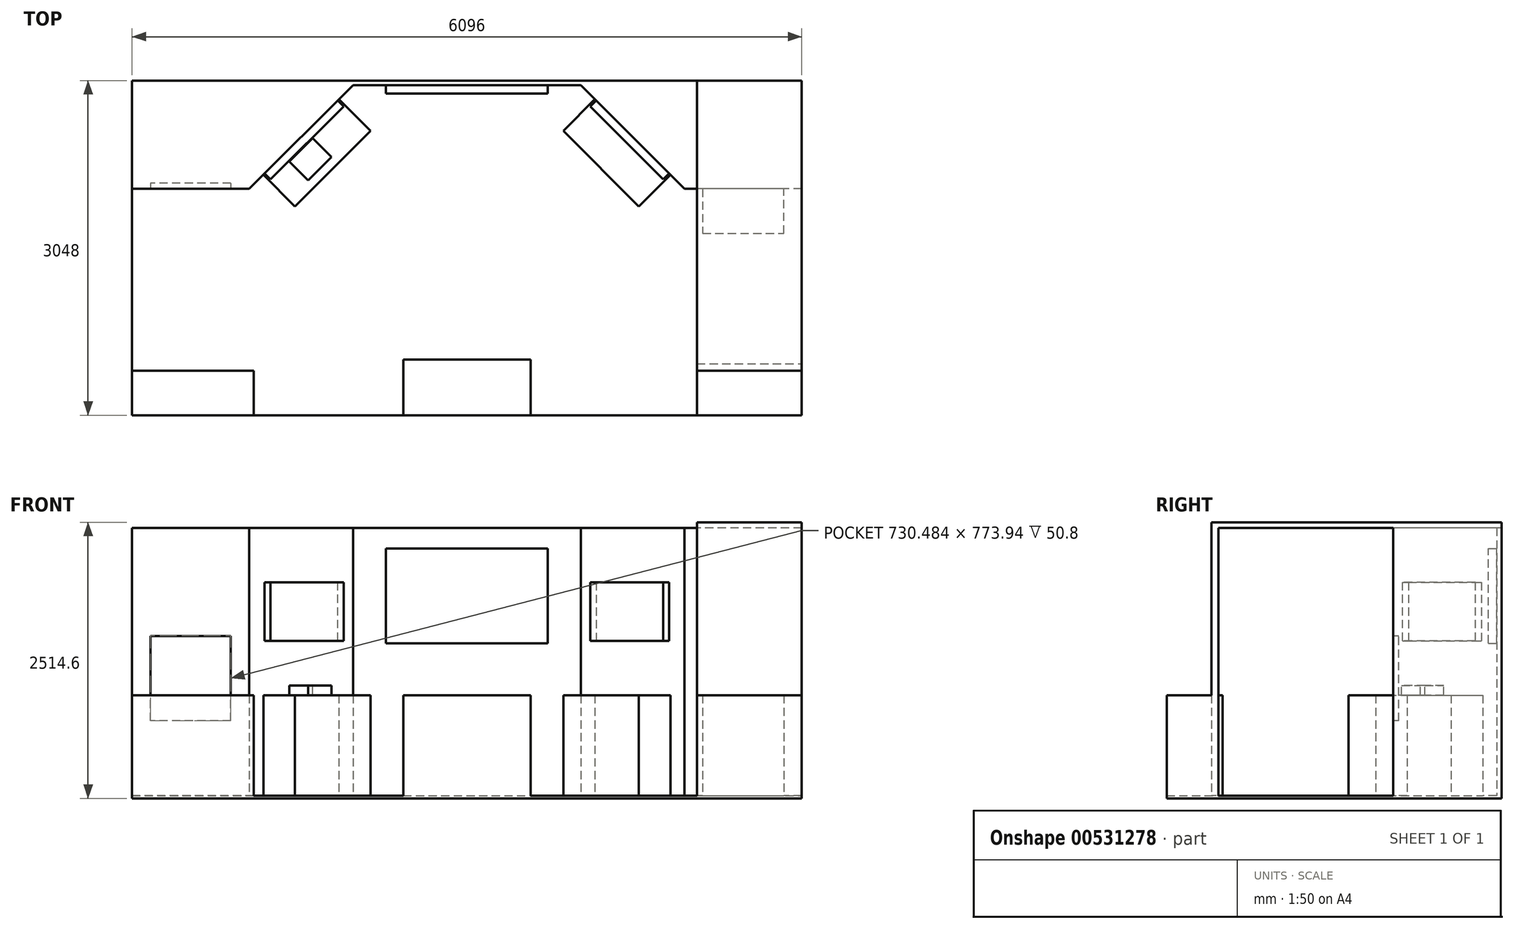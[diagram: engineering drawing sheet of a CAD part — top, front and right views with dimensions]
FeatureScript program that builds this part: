
annotation { "Feature Type Name" : "Feature", "Feature Type Description" : "" }
export const myFeature = defineFeature(function(context is Context, id is Id, definition is map)
    precondition{}
    {
        {
            var Q0;
            Q0=qCreatedBy(makeId("Top.planeOp"),FACE);
            var sketch = newSketch(context, id + "F0", { "sketchPlane" : qUnion([Q0])});
            skLineSegment(sketch, "E0.bottom", {"start": v(3048, 1524) * mm, "end": v(-3048, 1524) * mm});
            skLineSegment(sketch, "E0.top", {"start": v(3048, -1524) * mm, "end": v(-3048, -1524) * mm});
            skLineSegment(sketch, "E0.left", {"start": v(3048, 1524) * mm, "end": v(3048, -1524) * mm});
            skLineSegment(sketch, "E0.right", {"start": v(-3048, 1524) * mm, "end": v(-3048, -1524) * mm});
            skPoint(sketch, "E0.middle", {"position": v(0, 0) * mm});
            skSolve(sketch);
        }
        {
            var Q0;
            Q0=makeQuery(id+"F0.imprint","IMPRINT",FACE,{"disambiguationData":[TD([[makeQuery(id+"F0.imprint","IMPRINT",EDGE,{"derivedFrom":sQuery(id+"F0.wireOp",EDGE,"E0.bottom")}),1.0]])]});
            var sketch = newSketch(context, id + "F1", { "sketchPlane" : qUnion([Q0])});
            skLineSegment(sketch, "E1", {"start": v(3048, 1524) * mm, "end": v(-3048, 1524) * mm});
            skLineSegment(sketch, "E2", {"start": v(-3048, 1524) * mm, "end": v(-3048, 537.06) * mm});
            skLineSegment(sketch, "E3", {"start": v(-3048, 537.06) * mm, "end": v(-1981.2, 537.06) * mm});
            skLineSegment(sketch, "E4", {"start": v(-1981.2, 537.06) * mm, "end": v(-1037.42, 1480.84) * mm});
            skLineSegment(sketch, "E5", {"start": v(-1037.42, 1480.84) * mm, "end": v(1037.42, 1480.84) * mm});
            skLineSegment(sketch, "E6", {"start": v(1037.42, 1480.84) * mm, "end": v(1981.2, 537.06) * mm});
            skLineSegment(sketch, "E7", {"start": v(3048, 1524) * mm, "end": v(3048, 537.06) * mm});
            skLineSegment(sketch, "E8", {"start": v(3048, 537.06) * mm, "end": v(1981.2, 537.06) * mm});
            skLineSegment(sketch, "E9", {"start": v(0, 0) * mm, "end": v(0, 1480.84) * mm, "construction": true});
            skLineSegment(sketch, "E10", {"start": v(-1853.34, 664.91) * mm, "end": v(-1565.97, 377.55) * mm});
            skLineSegment(sketch, "E11", {"start": v(-1565.97, 377.55) * mm, "end": v(-877.9, 1065.61) * mm});
            skLineSegment(sketch, "E12", {"start": v(-877.9, 1065.61) * mm, "end": v(-1165.27, 1352.98) * mm});
            skLineSegment(sketch, "E13", {"start": v(1165.27, 1352.98) * mm, "end": v(877.9, 1065.61) * mm});
            skLineSegment(sketch, "E14", {"start": v(877.9, 1065.61) * mm, "end": v(1565.97, 377.55) * mm});
            skLineSegment(sketch, "E15", {"start": v(1565.97, 377.55) * mm, "end": v(1853.34, 664.91) * mm});
            skLineSegment(sketch, "E16", {"start": v(2145.45, 537.06) * mm, "end": v(2145.45, 130.66) * mm});
            skLineSegment(sketch, "E17", {"start": v(2145.45, 130.66) * mm, "end": v(2883.75, 130.66) * mm});
            skLineSegment(sketch, "E18", {"start": v(2883.75, 130.66) * mm, "end": v(2883.75, 537.06) * mm});
            skLineSegment(sketch, "E19", {"start": v(-1509.3, 1008.95) * mm, "end": v(-1221.94, 721.58) * mm, "construction": true});
            skLineSegment(sketch, "E20", {"start": v(1509.3, 1008.95) * mm, "end": v(1221.94, 721.58) * mm, "construction": true});
            skLineSegment(sketch, "E21", {"start": v(2514.6, 537.06) * mm, "end": v(2514.6, 130.66) * mm, "construction": true});
            skLineSegment(sketch, "E22.bottom", {"start": v(3048, -1524) * mm, "end": v(2094.08, -1524) * mm});
            skLineSegment(sketch, "E22.top", {"start": v(3048, -648) * mm, "end": v(2094.08, -648) * mm});
            skLineSegment(sketch, "E22.left", {"start": v(3048, -1524) * mm, "end": v(3048, -648) * mm});
            skLineSegment(sketch, "E22.right", {"start": v(2094.08, -1524) * mm, "end": v(2094.08, -648) * mm});
            skLineSegment(sketch, "E23", {"start": v(2094.08, -1086) * mm, "end": v(3048, -1086) * mm, "construction": true});
            skLineSegment(sketch, "E24.bottom", {"start": v(2094.08, -1117.6) * mm, "end": v(3048, -1117.6) * mm});
            skLineSegment(sketch, "E24.top", {"start": v(2094.08, -1054.4) * mm, "end": v(3048, -1054.4) * mm});
            skLineSegment(sketch, "E24.left", {"start": v(2094.08, -1054.4) * mm, "end": v(2094.08, -1117.6) * mm});
            skLineSegment(sketch, "E24.right", {"start": v(3048, -1054.4) * mm, "end": v(3048, -1117.6) * mm});
            skPoint(sketch, "E24.middle", {"position": v(2571.04, -1086) * mm});
            skLineSegment(sketch, "E25.bottom", {"start": v(579.49, -1524) * mm, "end": v(-579.49, -1524) * mm});
            skLineSegment(sketch, "E25.top", {"start": v(579.49, -1016) * mm, "end": v(-579.49, -1016) * mm});
            skLineSegment(sketch, "E25.left", {"start": v(579.49, -1524) * mm, "end": v(579.49, -1016) * mm});
            skLineSegment(sketch, "E25.right", {"start": v(-579.49, -1524) * mm, "end": v(-579.49, -1016) * mm});
            skPoint(sketch, "E25.middle", {"position": v(0, -1270) * mm});
            skLineSegment(sketch, "E26", {"start": v(0, -1270) * mm, "end": v(0, 0) * mm, "construction": true});
            skSolve(sketch);
        }
        {
            var Q0;
            Q0=makeQuery(id+"F1.imprint","IMPRINT",FACE,{"disambiguationData":[TD([[makeQuery(id+"F1.imprint","IMPRINT",EDGE,{"derivedFrom":sQuery(id+"F1.wireOp",EDGE,"E1")}),1.0]])]});
            var Q1;
            Q1=makeQuery(id+"F1.imprint","IMPRINT",FACE,{"disambiguationData":[TD([[makeQuery(id+"F1.imprint","IMPRINT",EDGE,{"derivedFrom":sQuery(id+"F1.wireOp",EDGE,"E24.bottom")}),1.0]])]});
            extrude(context, id + "F2", {"entities" : qUnion([Q0, Q1]), "depth" : 2438.4 * mm, "offsetDistance" : 25.4 * mm});
        }
        {
            var Q0;
            {var subQ0=sQuery(id+"F1.wireOp",EDGE,"E10");Q0=makeQuery(id+"F1.imprint","IMPRINT",FACE,{"disambiguationData":[TD([[makeQuery(id+"F1.imprint","IMPRINT",EDGE,{"derivedFrom":subQ0}),1.0]])]});}
            var Q1;
            Q1=makeQuery(id+"F1.imprint","IMPRINT",FACE,{"disambiguationData":[TD([[makeQuery(id+"F1.imprint","IMPRINT",EDGE,{"derivedFrom":sQuery(id+"F1.wireOp",EDGE,"E25.bottom")}),-1.0]])]});
            var Q2;
            {var subQ0=sQuery(id+"F1.wireOp",EDGE,"E13");Q2=makeQuery(id+"F1.imprint","IMPRINT",FACE,{"disambiguationData":[TD([[makeQuery(id+"F1.imprint","IMPRINT",EDGE,{"derivedFrom":subQ0}),1.0]])]});}
            var Q3;
            {var subQ0=sQuery(id+"F1.wireOp",EDGE,"E16");Q3=makeQuery(id+"F1.imprint","IMPRINT",FACE,{"disambiguationData":[TD([[makeQuery(id+"F1.imprint","IMPRINT",EDGE,{"derivedFrom":subQ0}),1.0]])]});}
            var Q4;
            {var subQ0=sQuery(id+"F1.wireOp",EDGE,"E22.bottom");Q4=makeQuery(id+"F1.imprint","IMPRINT",FACE,{"disambiguationData":[TD([[makeQuery(id+"F1.imprint","IMPRINT",EDGE,{"derivedFrom":subQ0}),-1.0]])]});}
            extrude(context, id + "F3", {"entities" : qUnion([Q0, Q1, Q2, Q3, Q4]), "operationType" : NewBodyOperationType.ADD, "depth" : 914.4 * mm, "offsetDistance" : 25.4 * mm});
        }
        {
            var Q0;
            Q0=makeQuery(id+"F0.imprint","IMPRINT",FACE,{"disambiguationData":[TD([[makeQuery(id+"F0.imprint","IMPRINT",EDGE,{"derivedFrom":sQuery(id+"F0.wireOp",EDGE,"E0.bottom")}),1.0]])]});
            extrude(context, id + "F4", {"entities" : qUnion([Q0]), "operationType" : NewBodyOperationType.ADD, "oppositeDirection" : true, "depth" : 25.4 * mm, "offsetDistance" : 25.4 * mm});
        }
        {
            var Q0;
            Q0=makeQuery(id+"F2.opExtrude","CAP_FACE",FACE,{"disambiguationData":[OSD([sQuery(id+"F1.wireOp",EDGE,"E1"),sQuery(id+"F1.wireOp",EDGE,"E2"),sQuery(id+"F1.wireOp",EDGE,"E3"),sQuery(id+"F1.wireOp",EDGE,"E4"),sQuery(id+"F1.wireOp",EDGE,"E5"),sQuery(id+"F1.wireOp",EDGE,"E6"),sQuery(id+"F1.wireOp",EDGE,"E7"),sQuery(id+"F1.wireOp",EDGE,"E8")])],"isStart":false});
            var sketch = newSketch(context, id + "F5", { "sketchPlane" : qUnion([Q0])});
            skLineSegment(sketch, "E27.bottom", {"start": v(3048, 1524) * mm, "end": v(2094.08, 1524) * mm});
            skLineSegment(sketch, "E27.top", {"start": v(3048, -1117.6) * mm, "end": v(2094.08, -1117.6) * mm});
            skLineSegment(sketch, "E27.left", {"start": v(3048, 1524) * mm, "end": v(3048, -1117.6) * mm});
            skLineSegment(sketch, "E27.right", {"start": v(2094.08, 1524) * mm, "end": v(2094.08, -1117.6) * mm});
            skSolve(sketch);
        }
        {
            var Q0;
            {var subQ0=sQuery(id+"F5.wireOp",EDGE,"E27.top");Q0=makeQuery(id+"F5.imprint","IMPRINT",FACE,{"disambiguationData":[TD([[makeQuery(id+"F5.imprint","IMPRINT",EDGE,{"derivedFrom":subQ0}),-1.0]])]});}
            var Q1;
            {var subQ0=sQuery(id+"F5.wireOp",EDGE,"E27.bottom");Q1=makeQuery(id+"F5.imprint","IMPRINT",FACE,{"disambiguationData":[TD([[makeQuery(id+"F5.imprint","IMPRINT",EDGE,{"derivedFrom":subQ0}),1.0]])]});}
            extrude(context, id + "F6", {"entities" : qUnion([Q0, Q1]), "operationType" : NewBodyOperationType.ADD, "depth" : 50.8 * mm, "offsetDistance" : 25.4 * mm});
        }
        {
            var Q0;
            Q0=makeQuery(id+"F2.opExtrude","SWEPT_FACE",FACE,{"disambiguationData":[OSD([sQuery(id+"F1.wireOp",EDGE,"E5")])]});
            var sketch = newSketch(context, id + "F7", { "sketchPlane" : qUnion([Q0])});
            skLineSegment(sketch, "E28.bottom", {"start": v(736.6, 1386.04) * mm, "end": v(-736.6, 1386.04) * mm});
            skLineSegment(sketch, "E28.top", {"start": v(736.6, 2249.64) * mm, "end": v(-736.6, 2249.64) * mm});
            skLineSegment(sketch, "E28.left", {"start": v(736.6, 1386.04) * mm, "end": v(736.6, 2249.64) * mm});
            skLineSegment(sketch, "E28.right", {"start": v(-736.6, 1386.04) * mm, "end": v(-736.6, 2249.64) * mm});
            skPoint(sketch, "E28.middle", {"position": v(0, 1817.84) * mm});
            skLineSegment(sketch, "E29", {"start": v(0, 2438.4) * mm, "end": v(0, 1817.84) * mm, "construction": true});
            skSolve(sketch);
        }
        {
            var Q0;
            Q0=makeQuery(id+"F7.imprint","IMPRINT",FACE,{"disambiguationData":[TD([[makeQuery(id+"F7.imprint","IMPRINT",EDGE,{"derivedFrom":sQuery(id+"F7.wireOp",EDGE,"E28.bottom")}),-1.0]])]});
            extrude(context, id + "F8", {"entities" : qUnion([Q0]), "operationType" : NewBodyOperationType.ADD, "depth" : 76.2 * mm, "offsetDistance" : 25.4 * mm});
        }
        {
            var Q0;
            Q0=makeQuery(id+"F2.opExtrude","SWEPT_FACE",FACE,{"disambiguationData":[OSD([sQuery(id+"F1.wireOp",EDGE,"E4")])]});
            var sketch = newSketch(context, id + "F9", { "sketchPlane" : qUnion([Q0])});
            skLineSegment(sketch, "E30.bottom", {"start": v(116.1, 1409.7) * mm, "end": v(-823.7, 1409.7) * mm});
            skLineSegment(sketch, "E30.top", {"start": v(116.1, 1943.1) * mm, "end": v(-823.7, 1943.1) * mm});
            skLineSegment(sketch, "E30.left", {"start": v(116.1, 1409.7) * mm, "end": v(116.1, 1943.1) * mm});
            skLineSegment(sketch, "E30.right", {"start": v(-823.7, 1409.7) * mm, "end": v(-823.7, 1943.1) * mm});
            skPoint(sketch, "E30.middle", {"position": v(-353.8, 1676.4) * mm});
            skSolve(sketch);
        }
        {
            var Q0;
            Q0=makeQuery(id+"F2.opExtrude","SWEPT_FACE",FACE,{"disambiguationData":[OSD([sQuery(id+"F1.wireOp",EDGE,"E6")])]});
            var sketch = newSketch(context, id + "F10", { "sketchPlane" : qUnion([Q0])});
            skLineSegment(sketch, "E31.bottom", {"start": v(823.7, 1943.1) * mm, "end": v(-116.1, 1943.1) * mm});
            skLineSegment(sketch, "E31.top", {"start": v(823.7, 1409.7) * mm, "end": v(-116.1, 1409.7) * mm});
            skLineSegment(sketch, "E31.left", {"start": v(823.7, 1943.1) * mm, "end": v(823.7, 1409.7) * mm});
            skLineSegment(sketch, "E31.right", {"start": v(-116.1, 1943.1) * mm, "end": v(-116.1, 1409.7) * mm});
            skPoint(sketch, "E31.middle", {"position": v(353.8, 1676.4) * mm});
            skSolve(sketch);
        }
        {
            var Q0;
            Q0=makeQuery(id+"F9.imprint","IMPRINT",FACE,{"disambiguationData":[TD([[makeQuery(id+"F9.imprint","IMPRINT",EDGE,{"derivedFrom":sQuery(id+"F9.wireOp",EDGE,"E30.bottom")}),-1.0]])]});
            extrude(context, id + "F11", {"entities" : qUnion([Q0]), "operationType" : NewBodyOperationType.ADD, "depth" : 76.2 * mm, "offsetDistance" : 25.4 * mm});
        }
        {
            var Q0;
            Q0=makeQuery(id+"F10.imprint","IMPRINT",FACE,{"disambiguationData":[TD([[makeQuery(id+"F10.imprint","IMPRINT",EDGE,{"derivedFrom":sQuery(id+"F10.wireOp",EDGE,"E31.bottom")}),1.0]])]});
            extrude(context, id + "F12", {"entities" : qUnion([Q0]), "operationType" : NewBodyOperationType.ADD, "depth" : 76.2 * mm, "offsetDistance" : 25.4 * mm});
        }
        {
            var Q0;
            Q0=makeQuery(id+"F2.opExtrude","SWEPT_FACE",FACE,{"disambiguationData":[OSD([sQuery(id+"F1.wireOp",EDGE,"E3")])]});
            var sketch = newSketch(context, id + "F13", { "sketchPlane" : qUnion([Q0])});
            skLineSegment(sketch, "E32.bottom", {"start": v(-2149.36, 680.56) * mm, "end": v(-2879.84, 680.56) * mm});
            skLineSegment(sketch, "E32.top", {"start": v(-2149.36, 1454.5) * mm, "end": v(-2879.84, 1454.5) * mm});
            skLineSegment(sketch, "E32.left", {"start": v(-2149.36, 680.56) * mm, "end": v(-2149.36, 1454.5) * mm});
            skLineSegment(sketch, "E32.right", {"start": v(-2879.84, 680.56) * mm, "end": v(-2879.84, 1454.5) * mm});
            skPoint(sketch, "E32.middle", {"position": v(-2514.6, 1067.53) * mm});
            skSolve(sketch);
        }
        {
            var Q0;
            Q0=makeQuery(id+"F13.imprint","IMPRINT",FACE,{"disambiguationData":[TD([[makeQuery(id+"F13.imprint","IMPRINT",EDGE,{"derivedFrom":sQuery(id+"F13.wireOp",EDGE,"E32.bottom")}),-1.0]])]});
            extrude(context, id + "F14", {"entities" : qUnion([Q0]), "operationType" : NewBodyOperationType.REMOVE, "oppositeDirection" : true, "depth" : 50.8 * mm, "offsetDistance" : 25.4 * mm});
        }
        {
            var Q0;
            Q0=makeQuery(id+"F3.opExtrude","SWEPT_FACE",FACE,{"disambiguationData":[OSD([sQuery(id+"F1.wireOp",EDGE,"E10")])]});
            var sketch = newSketch(context, id + "F15", { "sketchPlane" : qUnion([Q0])});
            skLineSegment(sketch, "E33.bottom", {"start": v(-1456.83, 914.4) * mm, "end": v(-1698.13, 914.4) * mm});
            skLineSegment(sketch, "E33.top", {"start": v(-1456.83, 1003.3) * mm, "end": v(-1698.13, 1003.3) * mm});
            skLineSegment(sketch, "E33.left", {"start": v(-1456.83, 914.4) * mm, "end": v(-1456.83, 1003.3) * mm});
            skLineSegment(sketch, "E33.right", {"start": v(-1698.13, 914.4) * mm, "end": v(-1698.13, 1003.3) * mm});
            skPoint(sketch, "E33.middle", {"position": v(-1577.48, 958.85) * mm});
            skSolve(sketch);
        }
        {
            var Q0;
            Q0=makeQuery(id+"F15.imprint","IMPRINT",FACE,{"disambiguationData":[TD([[makeQuery(id+"F15.imprint","IMPRINT",EDGE,{"derivedFrom":sQuery(id+"F15.wireOp",EDGE,"E33.bottom")}),1.0]])]});
            extrude(context, id + "F16", {"entities" : qUnion([Q0]), "operationType" : NewBodyOperationType.ADD, "oppositeDirection" : true, "depth" : 553.72 * mm, "offsetDistance" : 25.4 * mm, "hasSecondDirection" : true, "secondDirectionOppositeDirection" : true, "secondDirectionDepth" : 254 * mm});
        }
        {
            var Q0;
            Q0=makeQuery(id+"F4.opExtrude","CAP_FACE",FACE,{"disambiguationData":[OSD([sQuery(id+"F0.wireOp",EDGE,"E0.bottom"),sQuery(id+"F0.wireOp",EDGE,"E0.top"),sQuery(id+"F0.wireOp",EDGE,"E0.left"),sQuery(id+"F0.wireOp",EDGE,"E0.right")])],"isStart":true});
            var sketch = newSketch(context, id + "F17", { "sketchPlane" : qUnion([Q0])});
            skLineSegment(sketch, "E34.bottom", {"start": v(-3048, -1524) * mm, "end": v(-1941.2, -1524) * mm});
            skLineSegment(sketch, "E34.top", {"start": v(-3048, -660.4) * mm, "end": v(-1941.2, -660.4) * mm});
            skLineSegment(sketch, "E34.left", {"start": v(-3048, -1524) * mm, "end": v(-3048, -660.4) * mm});
            skLineSegment(sketch, "E34.right", {"start": v(-1941.2, -1524) * mm, "end": v(-1941.2, -660.4) * mm});
            skLineSegment(sketch, "E35", {"start": v(-1941.2, -1092.2) * mm, "end": v(-3048, -1092.2) * mm, "construction": true});
            skLineSegment(sketch, "E36.bottom", {"start": v(-1941.2, -1066.8) * mm, "end": v(-3048, -1066.8) * mm});
            skLineSegment(sketch, "E36.top", {"start": v(-1941.2, -1117.6) * mm, "end": v(-3048, -1117.6) * mm});
            skLineSegment(sketch, "E36.left", {"start": v(-1941.2, -1066.8) * mm, "end": v(-1941.2, -1117.6) * mm});
            skLineSegment(sketch, "E36.right", {"start": v(-3048, -1066.8) * mm, "end": v(-3048, -1117.6) * mm});
            skPoint(sketch, "E36.middle", {"position": v(-2494.6, -1092.2) * mm});
            skSolve(sketch);
        }
        {
            var Q0;
            {var subQ0=sQuery(id+"F17.wireOp",EDGE,"E34.bottom");Q0=makeQuery(id+"F17.imprint","IMPRINT",FACE,{"disambiguationData":[TD([[makeQuery(id+"F17.imprint","IMPRINT",EDGE,{"derivedFrom":subQ0}),-1.0]])]});}
            extrude(context, id + "F18", {"entities" : qUnion([Q0]), "operationType" : NewBodyOperationType.ADD, "depth" : 914.4 * mm, "offsetDistance" : 25.4 * mm});
        }
    });
